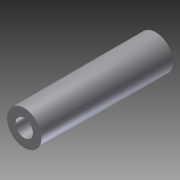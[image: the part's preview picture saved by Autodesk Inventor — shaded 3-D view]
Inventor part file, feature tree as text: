
AUTODESK INVENTOR PART (.ipt)
format: ipt  version: 2012 (Build 160160000, 160)  size: 79,872 bytes
history: native  units: in
note: dims shown in document units (in); Inventor stores cm internally (conversion verified against a paired STEP export)
features: extrude x1, sketch x1
ambient origin geometry x8: Origin, YZ Plane, XZ Plane, XY Plane, X Axis, Y Axis, Z Axis, Center Point
bodies: Solid1 (feature_tree)
feature tree (2):
  extrude  "Extrusion1"  Depth=0.198in
  sketch  "Sketch1"  dims[d0=0.3937in d1=0.198in d2=1.5in d3=0.0in]
